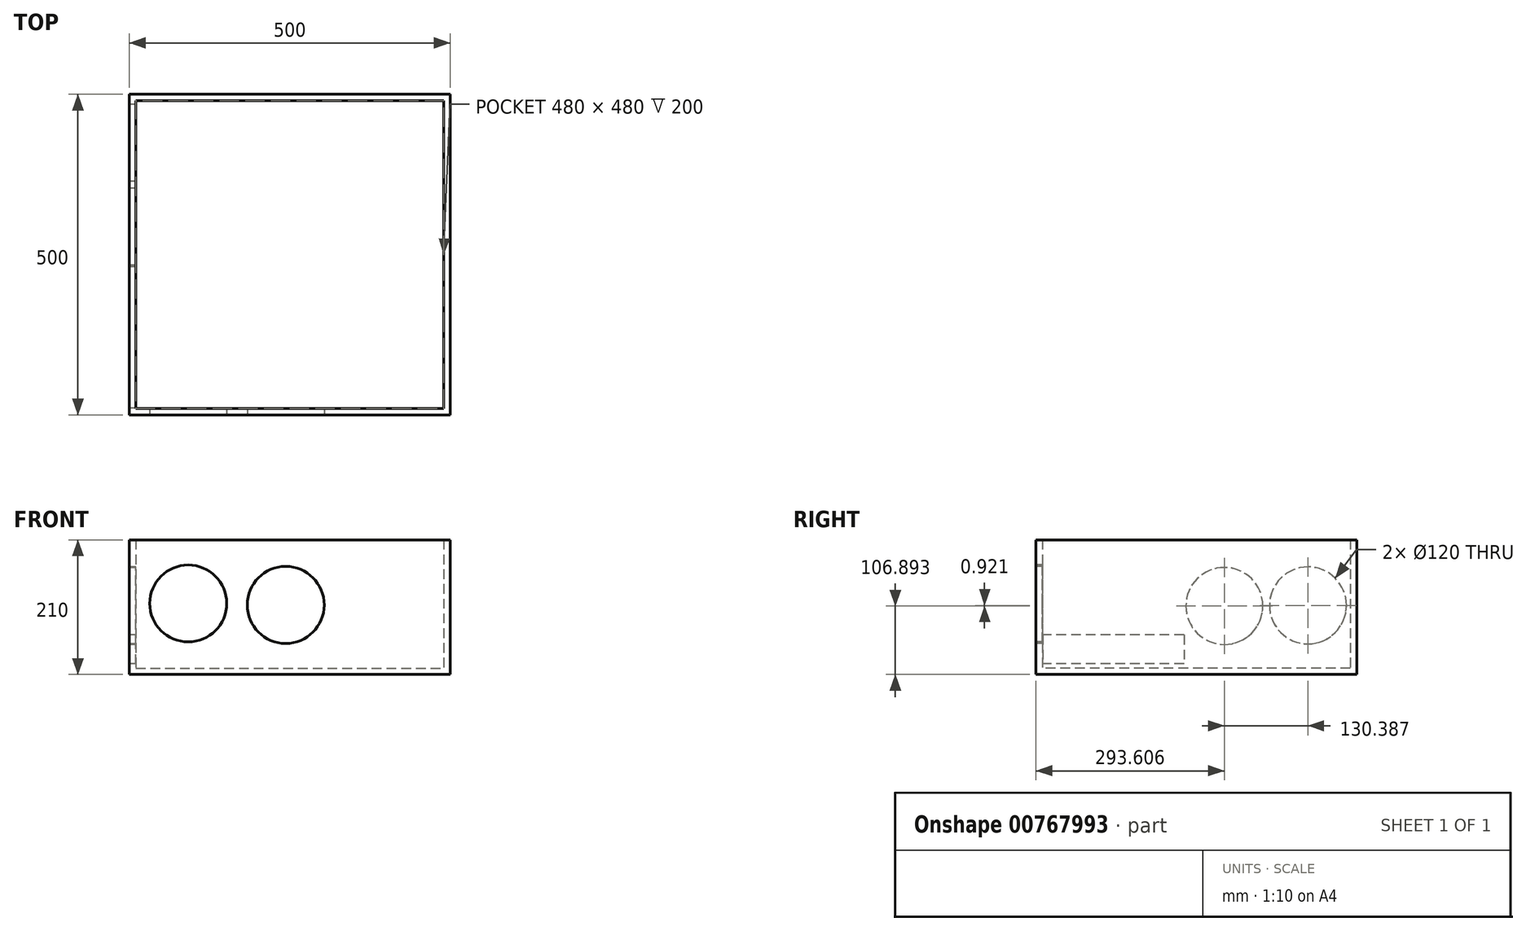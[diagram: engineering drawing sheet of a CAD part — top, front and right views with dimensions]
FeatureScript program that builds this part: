
annotation { "Feature Type Name" : "Feature", "Feature Type Description" : "" }
export const myFeature = defineFeature(function(context is Context, id is Id, definition is map)
    precondition{}
    {
        {
            var Q0;
            Q0=qCreatedBy(makeId("Top.planeOp"),FACE);
            var sketch = newSketch(context, id + "F0", { "sketchPlane" : qUnion([Q0])});
            skLineSegment(sketch, "E0.bottom", {"start": v(-448.41, 469.1) * mm, "end": v(51.59, 469.1) * mm});
            skLineSegment(sketch, "E0.top", {"start": v(-448.41, -30.9) * mm, "end": v(51.59, -30.9) * mm});
            skLineSegment(sketch, "E0.left", {"start": v(-448.41, 469.1) * mm, "end": v(-448.41, -30.9) * mm});
            skLineSegment(sketch, "E0.right", {"start": v(51.59, 469.1) * mm, "end": v(51.59, -30.9) * mm});
            skSolve(sketch);
        }
        {
            var Q0;
            Q0=makeQuery(id+"F0.imprint","IMPRINT",FACE,{"disambiguationData":[TD([[makeQuery(id+"F0.imprint","IMPRINT",EDGE,{"derivedFrom":sQuery(id+"F0.wireOp",EDGE,"E0.bottom")}),-1.0]])]});
            extrude(context, id + "F1", {"entities" : qUnion([Q0]), "depth" : 10 * mm, "offsetDistance" : 25 * mm});
        }
        {
            var Q0;
            Q0=makeQuery(id+"F1.opExtrude","CAP_FACE",FACE,{"disambiguationData":[OSD([sQuery(id+"F0.wireOp",EDGE,"E0.bottom"),sQuery(id+"F0.wireOp",EDGE,"E0.top"),sQuery(id+"F0.wireOp",EDGE,"E0.left"),sQuery(id+"F0.wireOp",EDGE,"E0.right")])],"isStart":false});
            var sketch = newSketch(context, id + "F2", { "sketchPlane" : qUnion([Q0])});
            skLineSegment(sketch, "E1.bottom", {"start": v(-448.41, 469.1) * mm, "end": v(51.59, 469.1) * mm});
            skLineSegment(sketch, "E1.top", {"start": v(-448.41, 459.1) * mm, "end": v(51.59, 459.1) * mm});
            skLineSegment(sketch, "E1.left", {"start": v(-448.41, 469.1) * mm, "end": v(-448.41, 459.1) * mm});
            skLineSegment(sketch, "E1.right", {"start": v(51.59, 469.1) * mm, "end": v(51.59, 459.1) * mm});
            skSolve(sketch);
        }
        {
            var Q0;
            Q0=makeQuery(id+"F2.imprint","IMPRINT",FACE,{"disambiguationData":[TD([[makeQuery(id+"F2.imprint","IMPRINT",EDGE,{"derivedFrom":sQuery(id+"F2.wireOp",EDGE,"E1.bottom")}),-1.0]])]});
            extrude(context, id + "F3", {"entities" : qUnion([Q0]), "operationType" : NewBodyOperationType.ADD, "depth" : 200 * mm, "offsetDistance" : 25 * mm});
        }
        {
            var Q0;
            Q0=makeQuery(id+"F1.opExtrude","CAP_FACE",FACE,{"disambiguationData":[OSD([sQuery(id+"F0.wireOp",EDGE,"E0.bottom"),sQuery(id+"F0.wireOp",EDGE,"E0.top"),sQuery(id+"F0.wireOp",EDGE,"E0.left"),sQuery(id+"F0.wireOp",EDGE,"E0.right")])],"isStart":false});
            var sketch = newSketch(context, id + "F4", { "sketchPlane" : qUnion([Q0])});
            skLineSegment(sketch, "E2.bottom", {"start": v(51.59, 459.1) * mm, "end": v(41.59, 459.1) * mm});
            skLineSegment(sketch, "E2.top", {"start": v(51.59, -30.9) * mm, "end": v(41.59, -30.9) * mm});
            skLineSegment(sketch, "E2.left", {"start": v(51.59, 459.1) * mm, "end": v(51.59, -30.9) * mm});
            skLineSegment(sketch, "E2.right", {"start": v(41.59, 459.1) * mm, "end": v(41.59, -30.9) * mm});
            skSolve(sketch);
        }
        {
            var Q0;
            Q0=makeQuery(id+"F4.imprint","IMPRINT",FACE,{"disambiguationData":[TD([[makeQuery(id+"F4.imprint","IMPRINT",EDGE,{"derivedFrom":sQuery(id+"F4.wireOp",EDGE,"E2.bottom")}),-1.0]])]});
            extrude(context, id + "F5", {"entities" : qUnion([Q0]), "operationType" : NewBodyOperationType.ADD, "depth" : 250 * mm, "offsetDistance" : 25 * mm});
        }
        {
            var Q0;
            Q0=makeQuery(id+"F1.opExtrude","CAP_FACE",FACE,{"disambiguationData":[OSD([sQuery(id+"F0.wireOp",EDGE,"E0.bottom"),sQuery(id+"F0.wireOp",EDGE,"E0.top"),sQuery(id+"F0.wireOp",EDGE,"E0.left"),sQuery(id+"F0.wireOp",EDGE,"E0.right")])],"isStart":false});
            var sketch = newSketch(context, id + "F6", { "sketchPlane" : qUnion([Q0])});
            skLineSegment(sketch, "E3.bottom", {"start": v(41.59, -30.9) * mm, "end": v(-448.41, -30.9) * mm});
            skLineSegment(sketch, "E3.top", {"start": v(41.59, -20.9) * mm, "end": v(-448.41, -20.9) * mm});
            skLineSegment(sketch, "E3.left", {"start": v(41.59, -30.9) * mm, "end": v(41.59, -20.9) * mm});
            skLineSegment(sketch, "E3.right", {"start": v(-448.41, -30.9) * mm, "end": v(-448.41, -20.9) * mm});
            skSolve(sketch);
        }
        {
            var Q0;
            Q0=makeQuery(id+"F6.imprint","IMPRINT",FACE,{"disambiguationData":[TD([[makeQuery(id+"F6.imprint","IMPRINT",EDGE,{"derivedFrom":sQuery(id+"F6.wireOp",EDGE,"E3.bottom")}),1.0]])]});
            extrude(context, id + "F7", {"entities" : qUnion([Q0]), "operationType" : NewBodyOperationType.ADD, "depth" : 250 * mm, "offsetDistance" : 25 * mm});
        }
        {
            var Q0;
            Q0=makeQuery(id+"F1.opExtrude","CAP_FACE",FACE,{"disambiguationData":[OSD([sQuery(id+"F0.wireOp",EDGE,"E0.bottom"),sQuery(id+"F0.wireOp",EDGE,"E0.top"),sQuery(id+"F0.wireOp",EDGE,"E0.left"),sQuery(id+"F0.wireOp",EDGE,"E0.right")])],"isStart":false});
            var sketch = newSketch(context, id + "F8", { "sketchPlane" : qUnion([Q0])});
            skLineSegment(sketch, "E4.bottom", {"start": v(-448.41, 459.1) * mm, "end": v(-438.41, 459.1) * mm});
            skLineSegment(sketch, "E4.top", {"start": v(-448.41, -20.9) * mm, "end": v(-438.41, -20.9) * mm});
            skLineSegment(sketch, "E4.left", {"start": v(-448.41, 459.1) * mm, "end": v(-448.41, -20.9) * mm});
            skLineSegment(sketch, "E4.right", {"start": v(-438.41, 459.1) * mm, "end": v(-438.41, -20.9) * mm});
            skSolve(sketch);
        }
        {
            var Q0;
            Q0=makeQuery(id+"F8.imprint","IMPRINT",FACE,{"disambiguationData":[TD([[makeQuery(id+"F8.imprint","IMPRINT",EDGE,{"derivedFrom":sQuery(id+"F8.wireOp",EDGE,"E4.bottom")}),-1.0]])]});
            extrude(context, id + "F9", {"entities" : qUnion([Q0]), "operationType" : NewBodyOperationType.ADD, "depth" : 250 * mm, "offsetDistance" : 25 * mm});
        }
        {
            var Q0;
            Q0=makeQuery(id+"F3.opExtrude","CAP_FACE",FACE,{"disambiguationData":[OSD([sQuery(id+"F2.wireOp",EDGE,"E1.bottom"),sQuery(id+"F2.wireOp",EDGE,"E1.top"),sQuery(id+"F2.wireOp",EDGE,"E1.left"),sQuery(id+"F2.wireOp",EDGE,"E1.right")])],"isStart":false});
            extrude(context, id + "F10", {"entities" : qUnion([Q0]), "operationType" : NewBodyOperationType.ADD, "depth" : 50 * mm, "offsetDistance" : 25 * mm});
        }
        {
            var Q0;
            Q0=makeQuery(id+"F10.boolean.opBoolean","MERGE",FACE,{"derivedFrom":[makeQuery(id+"F9.boolean.opBoolean","MERGE",FACE,{"derivedFrom":[makeQuery(id+"F7.boolean.opBoolean","MERGE",FACE,{"derivedFrom":[makeQuery(id+"F5.opExtrude","CAP_FACE",FACE,{"disambiguationData":[OSD([sQuery(id+"F4.wireOp",EDGE,"E2.bottom"),sQuery(id+"F4.wireOp",EDGE,"E2.top"),sQuery(id+"F4.wireOp",EDGE,"E2.left"),sQuery(id+"F4.wireOp",EDGE,"E2.right")])],"isStart":false}),makeQuery(id+"F7.opExtrude","CAP_FACE",FACE,{"disambiguationData":[OSD([sQuery(id+"F6.wireOp",EDGE,"E3.bottom"),sQuery(id+"F6.wireOp",EDGE,"E3.top"),sQuery(id+"F6.wireOp",EDGE,"E3.left"),sQuery(id+"F6.wireOp",EDGE,"E3.right")])],"isStart":false})]}),makeQuery(id+"F9.opExtrude","CAP_FACE",FACE,{"disambiguationData":[OSD([sQuery(id+"F8.wireOp",EDGE,"E4.bottom"),sQuery(id+"F8.wireOp",EDGE,"E4.top"),sQuery(id+"F8.wireOp",EDGE,"E4.left"),sQuery(id+"F8.wireOp",EDGE,"E4.right")])],"isStart":false})]}),makeQuery(id+"F10.opExtrude","CAP_FACE",FACE,{"disambiguationData":[OSD([sQuery(id+"F2.wireOp",EDGE,"E1.bottom"),sQuery(id+"F2.wireOp",EDGE,"E1.top"),sQuery(id+"F2.wireOp",EDGE,"E1.left"),sQuery(id+"F2.wireOp",EDGE,"E1.right")])],"isStart":false})]});
            extrude(context, id + "F11", {"entities" : qUnion([Q0]), "operationType" : NewBodyOperationType.REMOVE, "oppositeDirection" : true, "depth" : 50 * mm, "offsetDistance" : 25 * mm});
        }
        {
            var Q0;
            Q0=makeQuery(id+"F7.boolean.opBoolean","MERGE",FACE,{"derivedFrom":[makeQuery(id+"F5.boolean.opBoolean","MERGE",FACE,{"derivedFrom":[makeQuery(id+"F1.opExtrude","SWEPT_FACE",FACE,{"disambiguationData":[OSD([sQuery(id+"F0.wireOp",EDGE,"E0.top")])]}),makeQuery(id+"F5.opExtrude","SWEPT_FACE",FACE,{"disambiguationData":[OSD([sQuery(id+"F4.wireOp",EDGE,"E2.top")])]})]}),makeQuery(id+"F7.opExtrude","SWEPT_FACE",FACE,{"disambiguationData":[OSD([sQuery(id+"F6.wireOp",EDGE,"E3.bottom")])]})]});
            var sketch = newSketch(context, id + "F12", { "sketchPlane" : qUnion([Q0])});
            skCircle(sketch, "E5", {"center": v(-356.7, 110.87) * mm, "radius": 60 * mm});
            skSolve(sketch);
        }
        {
            var Q0;
            Q0=makeQuery(id+"F12.imprint","IMPRINT",FACE,{"disambiguationData":[TD([[makeQuery(id+"F12.imprint","IMPRINT",EDGE,{"derivedFrom":sQuery(id+"F12.wireOp",EDGE,"E5")}),1.0]])]});
            extrude(context, id + "F13", {"entities" : qUnion([Q0]), "operationType" : NewBodyOperationType.REMOVE, "oppositeDirection" : true, "depth" : 70 * mm, "offsetDistance" : 25 * mm});
        }
        {
            var Q0;
            Q0=makeQuery(id+"F7.boolean.opBoolean","MERGE",FACE,{"derivedFrom":[makeQuery(id+"F5.boolean.opBoolean","MERGE",FACE,{"derivedFrom":[makeQuery(id+"F1.opExtrude","SWEPT_FACE",FACE,{"disambiguationData":[OSD([sQuery(id+"F0.wireOp",EDGE,"E0.top")])]}),makeQuery(id+"F5.opExtrude","SWEPT_FACE",FACE,{"disambiguationData":[OSD([sQuery(id+"F4.wireOp",EDGE,"E2.top")])]})]}),makeQuery(id+"F7.opExtrude","SWEPT_FACE",FACE,{"disambiguationData":[OSD([sQuery(id+"F6.wireOp",EDGE,"E3.bottom")])]})]});
            var sketch = newSketch(context, id + "F14", { "sketchPlane" : qUnion([Q0])});
            skCircle(sketch, "E6", {"center": v(-204.66, 108.5) * mm, "radius": 60 * mm});
            skSolve(sketch);
        }
        {
            var Q0;
            Q0=makeQuery(id+"F14.imprint","IMPRINT",FACE,{"disambiguationData":[TD([[makeQuery(id+"F14.imprint","IMPRINT",EDGE,{"derivedFrom":sQuery(id+"F14.wireOp",EDGE,"E6")}),1.0]])]});
            extrude(context, id + "F15", {"entities" : qUnion([Q0]), "operationType" : NewBodyOperationType.REMOVE, "oppositeDirection" : true, "depth" : 122 * mm, "offsetDistance" : 25 * mm});
        }
        {
            var Q0;
            {var subQ0=sQuery(id+"F2.wireOp",EDGE,"E1.left");Q0=makeQuery(id+"F10.boolean.opBoolean","MERGE",FACE,{"derivedFrom":[makeQuery(id+"F9.boolean.opBoolean","MERGE",FACE,{"derivedFrom":[makeQuery(id+"F7.boolean.opBoolean","MERGE",FACE,{"derivedFrom":[makeQuery(id+"F3.boolean.opBoolean","MERGE",FACE,{"derivedFrom":[makeQuery(id+"F1.opExtrude","SWEPT_FACE",FACE,{"disambiguationData":[OSD([sQuery(id+"F0.wireOp",EDGE,"E0.left")])]}),makeQuery(id+"F3.opExtrude","SWEPT_FACE",FACE,{"disambiguationData":[OSD([subQ0])]})]}),makeQuery(id+"F7.opExtrude","SWEPT_FACE",FACE,{"disambiguationData":[OSD([sQuery(id+"F6.wireOp",EDGE,"E3.right")])]})]}),makeQuery(id+"F9.opExtrude","SWEPT_FACE",FACE,{"disambiguationData":[OSD([sQuery(id+"F8.wireOp",EDGE,"E4.left")])]})]}),makeQuery(id+"F10.opExtrude","SWEPT_FACE",FACE,{"disambiguationData":[OSD([subQ0])]})]});}
            var sketch = newSketch(context, id + "F16", { "sketchPlane" : qUnion([Q0])});
            skLineSegment(sketch, "E7.bottom", {"start": v(-199.82, 61.59) * mm, "end": v(20.18, 61.59) * mm});
            skLineSegment(sketch, "E7.top", {"start": v(-199.82, 16.59) * mm, "end": v(20.18, 16.59) * mm});
            skLineSegment(sketch, "E7.left", {"start": v(-199.82, 61.59) * mm, "end": v(-199.82, 16.59) * mm});
            skLineSegment(sketch, "E7.right", {"start": v(20.18, 61.59) * mm, "end": v(20.18, 16.59) * mm});
            skSolve(sketch);
        }
        {
            var Q0;
            Q0=makeQuery(id+"F16.imprint","IMPRINT",FACE,{"disambiguationData":[TD([[makeQuery(id+"F16.imprint","IMPRINT",EDGE,{"derivedFrom":sQuery(id+"F16.wireOp",EDGE,"E7.bottom")}),-1.0]])]});
            extrude(context, id + "F17", {"entities" : qUnion([Q0]), "operationType" : NewBodyOperationType.REMOVE, "oppositeDirection" : true, "depth" : 25 * mm, "offsetDistance" : 25 * mm});
        }
        {
            var Q0;
            {var subQ0=sQuery(id+"F2.wireOp",EDGE,"E1.left");Q0=makeQuery(id+"F10.boolean.opBoolean","MERGE",FACE,{"derivedFrom":[makeQuery(id+"F9.boolean.opBoolean","MERGE",FACE,{"derivedFrom":[makeQuery(id+"F7.boolean.opBoolean","MERGE",FACE,{"derivedFrom":[makeQuery(id+"F3.boolean.opBoolean","MERGE",FACE,{"derivedFrom":[makeQuery(id+"F1.opExtrude","SWEPT_FACE",FACE,{"disambiguationData":[OSD([sQuery(id+"F0.wireOp",EDGE,"E0.left")])]}),makeQuery(id+"F3.opExtrude","SWEPT_FACE",FACE,{"disambiguationData":[OSD([subQ0])]})]}),makeQuery(id+"F7.opExtrude","SWEPT_FACE",FACE,{"disambiguationData":[OSD([sQuery(id+"F6.wireOp",EDGE,"E3.right")])]})]}),makeQuery(id+"F9.opExtrude","SWEPT_FACE",FACE,{"disambiguationData":[OSD([sQuery(id+"F8.wireOp",EDGE,"E4.left")])]})]}),makeQuery(id+"F10.opExtrude","SWEPT_FACE",FACE,{"disambiguationData":[OSD([subQ0])]})]});}
            var sketch = newSketch(context, id + "F18", { "sketchPlane" : qUnion([Q0])});
            skCircle(sketch, "E8", {"center": v(-393.1, 107.81) * mm, "radius": 60 * mm});
            skCircle(sketch, "E9", {"center": v(-262.25, 112.42) * mm, "radius": 60 * mm});
            skSolve(sketch);
        }
        {
            var Q0;
            Q0=makeQuery(id+"F18.imprint","IMPRINT",FACE,{"disambiguationData":[TD([[makeQuery(id+"F18.imprint","IMPRINT",EDGE,{"derivedFrom":sQuery(id+"F18.wireOp",EDGE,"E8")}),1.0]])]});
            extrude(context, id + "F19", {"entities" : qUnion([Q0]), "operationType" : NewBodyOperationType.REMOVE, "oppositeDirection" : true, "depth" : 25 * mm, "offsetDistance" : 25 * mm});
        }
        {
            var Q0;
            {var subQ0=sQuery(id+"F2.wireOp",EDGE,"E1.left");Q0=makeQuery(id+"F10.boolean.opBoolean","MERGE",FACE,{"derivedFrom":[makeQuery(id+"F9.boolean.opBoolean","MERGE",FACE,{"derivedFrom":[makeQuery(id+"F7.boolean.opBoolean","MERGE",FACE,{"derivedFrom":[makeQuery(id+"F3.boolean.opBoolean","MERGE",FACE,{"derivedFrom":[makeQuery(id+"F1.opExtrude","SWEPT_FACE",FACE,{"disambiguationData":[OSD([sQuery(id+"F0.wireOp",EDGE,"E0.left")])]}),makeQuery(id+"F3.opExtrude","SWEPT_FACE",FACE,{"disambiguationData":[OSD([subQ0])]})]}),makeQuery(id+"F7.opExtrude","SWEPT_FACE",FACE,{"disambiguationData":[OSD([sQuery(id+"F6.wireOp",EDGE,"E3.right")])]})]}),makeQuery(id+"F9.opExtrude","SWEPT_FACE",FACE,{"disambiguationData":[OSD([sQuery(id+"F8.wireOp",EDGE,"E4.left")])]})]}),makeQuery(id+"F10.opExtrude","SWEPT_FACE",FACE,{"disambiguationData":[OSD([subQ0])]})]});}
            var sketch = newSketch(context, id + "F20", { "sketchPlane" : qUnion([Q0])});
            skCircle(sketch, "E10", {"center": v(-262.7, 106.9) * mm, "radius": 60 * mm});
            skSolve(sketch);
        }
        {
            var Q0;
            Q0=makeQuery(id+"F20.imprint","IMPRINT",FACE,{"disambiguationData":[TD([[makeQuery(id+"F20.imprint","IMPRINT",EDGE,{"derivedFrom":sQuery(id+"F20.wireOp",EDGE,"E10")}),1.0]])]});
            extrude(context, id + "F21", {"entities" : qUnion([Q0]), "operationType" : NewBodyOperationType.REMOVE, "oppositeDirection" : true, "depth" : 25 * mm, "offsetDistance" : 25 * mm});
        }
    });
